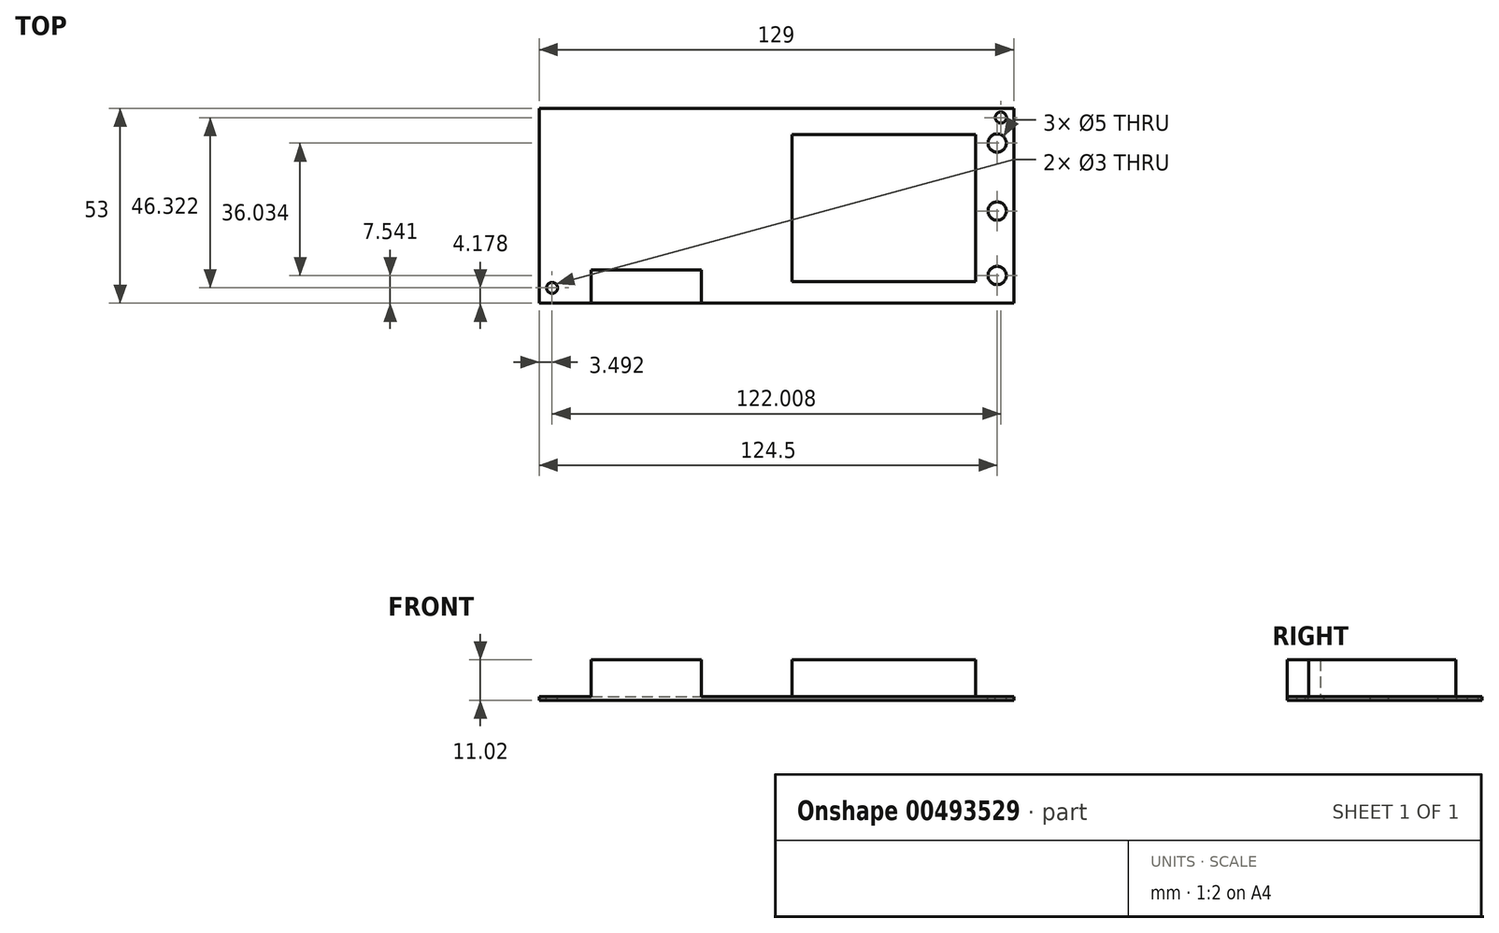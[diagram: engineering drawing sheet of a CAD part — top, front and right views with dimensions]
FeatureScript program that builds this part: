
annotation { "Feature Type Name" : "Feature", "Feature Type Description" : "" }
export const myFeature = defineFeature(function(context is Context, id is Id, definition is map)
    precondition{}
    {
        {
            var Q0;
            Q0=qCreatedBy(makeId("Top.planeOp"),FACE);
            var sketch = newSketch(context, id + "F0", { "sketchPlane" : qUnion([Q0])});
            skLineSegment(sketch, "E0.bottom", {"start": v(0, 0) * mm, "end": v(129, 0) * mm});
            skLineSegment(sketch, "E0.top", {"start": v(0, 53) * mm, "end": v(129, 53) * mm});
            skLineSegment(sketch, "E0.left", {"start": v(0, 0) * mm, "end": v(0, 53) * mm});
            skLineSegment(sketch, "E0.right", {"start": v(129, 0) * mm, "end": v(129, 53) * mm});
            skLineSegment(sketch, "E1.bottom", {"start": v(14.12, 0) * mm, "end": v(44.12, 0) * mm});
            skLineSegment(sketch, "E1.top", {"start": v(14.12, 9) * mm, "end": v(44.12, 9) * mm});
            skLineSegment(sketch, "E1.left", {"start": v(14.12, 0) * mm, "end": v(14.12, 9) * mm});
            skLineSegment(sketch, "E1.right", {"start": v(44.12, 0) * mm, "end": v(44.12, 9) * mm});
            skLineSegment(sketch, "E2.bottom", {"start": v(68.75, 45.92) * mm, "end": v(118.62, 45.92) * mm});
            skLineSegment(sketch, "E2.top", {"start": v(68.75, 5.92) * mm, "end": v(118.62, 5.92) * mm});
            skLineSegment(sketch, "E2.left", {"start": v(68.75, 45.92) * mm, "end": v(68.75, 5.92) * mm});
            skLineSegment(sketch, "E2.right", {"start": v(118.62, 45.92) * mm, "end": v(118.62, 5.92) * mm});
            skCircle(sketch, "E3", {"center": v(124.5, 43.57) * mm, "radius": 2.5 * mm});
            skCircle(sketch, "E4", {"center": v(124.5, 25.08) * mm, "radius": 2.5 * mm});
            skCircle(sketch, "E5", {"center": v(124.5, 7.54) * mm, "radius": 2.5 * mm});
            skCircle(sketch, "E6", {"center": v(125.5, 50.5) * mm, "radius": 1.5 * mm});
            skCircle(sketch, "E7", {"center": v(3.5, 4.18) * mm, "radius": 1.5 * mm});
            skSolve(sketch);
        }
        {
            var Q0;
            Q0=makeQuery(id+"F0.imprint","IMPRINT",FACE,{"disambiguationData":[TD([[makeQuery(id+"F0.imprint","IMPRINT",EDGE,{"derivedFrom":sQuery(id+"F0.wireOp",EDGE,"E0.top")}),-1.0]])]});
            var Q1;
            Q1=makeQuery(id+"F0.imprint","IMPRINT",FACE,{"disambiguationData":[TD([[makeQuery(id+"F0.imprint","IMPRINT",EDGE,{"derivedFrom":sQuery(id+"F0.wireOp",EDGE,"E2.bottom")}),-1.0]])]});
            var Q2;
            Q2=makeQuery(id+"F0.imprint","IMPRINT",FACE,{"disambiguationData":[TD([[makeQuery(id+"F0.imprint","IMPRINT",EDGE,{"derivedFrom":sQuery(id+"F0.wireOp",EDGE,"E1.top")}),-1.0]])]});
            extrude(context, id + "F1", {"entities" : qUnion([Q0, Q1, Q2]), "oppositeDirection" : true, "depth" : 1.02 * mm, "offsetDistance" : 25.4 * mm});
        }
        {
            var Q0;
            Q0=makeQuery(id+"F0.imprint","IMPRINT",FACE,{"disambiguationData":[TD([[makeQuery(id+"F0.imprint","IMPRINT",EDGE,{"derivedFrom":sQuery(id+"F0.wireOp",EDGE,"E1.top")}),-1.0]])]});
            var Q1;
            Q1=makeQuery(id+"F0.imprint","IMPRINT",FACE,{"disambiguationData":[TD([[makeQuery(id+"F0.imprint","IMPRINT",EDGE,{"derivedFrom":sQuery(id+"F0.wireOp",EDGE,"E2.bottom")}),-1.0]])]});
            extrude(context, id + "F2", {"entities" : qUnion([Q0, Q1]), "operationType" : NewBodyOperationType.ADD, "depth" : 10 * mm, "offsetDistance" : 25.4 * mm});
        }
    });
